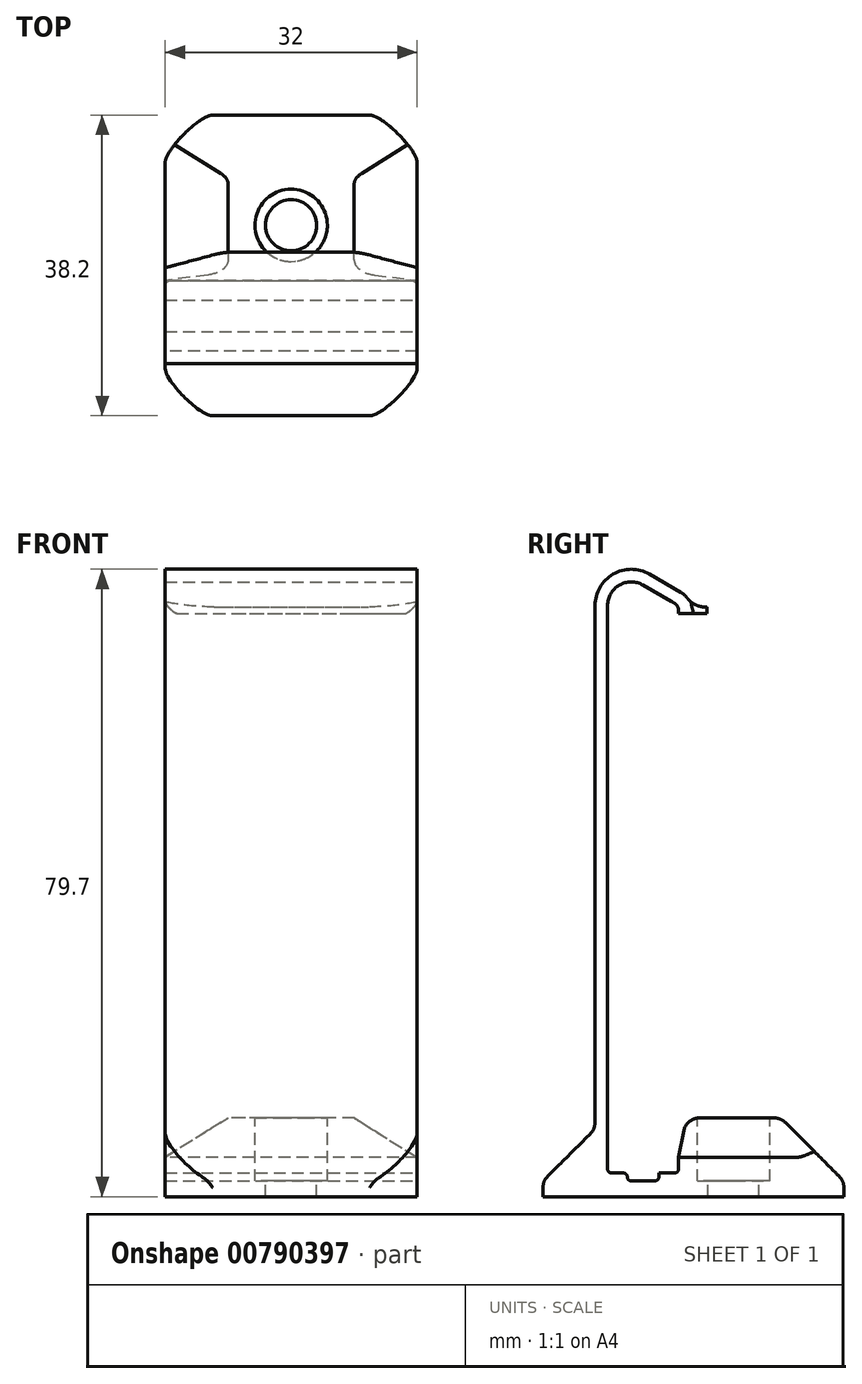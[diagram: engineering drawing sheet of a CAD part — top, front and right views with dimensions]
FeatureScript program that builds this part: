
annotation { "Feature Type Name" : "Feature", "Feature Type Description" : "" }
export const myFeature = defineFeature(function(context is Context, id is Id, definition is map)
    precondition{}
    {
        {
            var Q0;
            Q0=qCreatedBy(makeId("Right.planeOp"),FACE);
            var sketch = newSketch(context, id + "F0", { "sketchPlane" : qUnion([Q0])});
            skLineSegment(sketch, "E0.bottom", {"start": v(-4.5, 0) * mm, "end": v(4.5, 0) * mm});
            skLineSegment(sketch, "E0.top", {"start": v(-4.5, 72.1) * mm, "end": v(4.5, 72.1) * mm});
            skLineSegment(sketch, "E0.left", {"start": v(-4.5, 0) * mm, "end": v(-4.5, 72.1) * mm});
            skLineSegment(sketch, "E0.right", {"start": v(4.5, 0) * mm, "end": v(4.5, 72.1) * mm});
            skSolve(sketch);
        }
        {
            var Q0;
            Q0=qCreatedBy(makeId("Right.planeOp"),FACE);
            var sketch = newSketch(context, id + "F1", { "sketchPlane" : qUnion([Q0])});
            skLineSegment(sketch, "E1", {"start": v(-4.5, 5.6) * mm, "end": v(-6.1, 5.6) * mm});
            skLineSegment(sketch, "E2", {"start": v(-6.1, 5.6) * mm, "end": v(-12.7, -1) * mm});
            skLineSegment(sketch, "E3", {"start": v(-12.7, -1) * mm, "end": v(-12.7, -3) * mm});
            skLineSegment(sketch, "E4", {"start": v(-12.7, -3) * mm, "end": v(25.5, -3) * mm});
            skLineSegment(sketch, "E5", {"start": v(25.5, -3) * mm, "end": v(25.5, -1) * mm});
            skLineSegment(sketch, "E6", {"start": v(25.5, -1) * mm, "end": v(17.5, 7) * mm});
            skLineSegment(sketch, "E7", {"start": v(17.5, 7) * mm, "end": v(4.5, 7) * mm});
            skLineSegment(sketch, "E8", {"start": v(4.5, 7) * mm, "end": v(4.5, 0) * mm});
            skLineSegment(sketch, "E9", {"start": v(4.5, 0) * mm, "end": v(-4.5, 0) * mm});
            skLineSegment(sketch, "E10", {"start": v(-4.5, 0) * mm, "end": v(-4.5, 5.6) * mm});
            skSolve(sketch);
        }
        {
            var Q0;
            Q0=qSketchRegion(id+"F1",true);
            extrude(context, id + "F2", {"entities" : qUnion([Q0]), "endBound" : BoundingType.SYMMETRIC, "depth" : 32 * mm, "offsetDistance" : 25 * mm});
        }
        {
            var Q0;
            Q0=makeQuery(id+"F2.opExtrude","CAP_FACE",FACE,{"disambiguationData":[OSD([sQuery(id+"F1.wireOp",EDGE,"E1"),sQuery(id+"F1.wireOp",EDGE,"E2"),sQuery(id+"F1.wireOp",EDGE,"E3"),sQuery(id+"F1.wireOp",EDGE,"E4"),sQuery(id+"F1.wireOp",EDGE,"E5"),sQuery(id+"F1.wireOp",EDGE,"E6"),sQuery(id+"F1.wireOp",EDGE,"E7"),sQuery(id+"F1.wireOp",EDGE,"E8"),sQuery(id+"F1.wireOp",EDGE,"E9"),sQuery(id+"F1.wireOp",EDGE,"E10")])],"isStart":false});
            var sketch = newSketch(context, id + "F3", { "sketchPlane" : qUnion([Q0])});
            skLineSegment(sketch, "E11", {"start": v(-6.1, 5.6) * mm, "end": v(-4.5, 5.6) * mm});
            skLineSegment(sketch, "E12", {"start": v(-4.5, 5.6) * mm, "end": v(-4.5, 72.1) * mm});
            skLineSegment(sketch, "E13", {"start": v(0, 74.7) * mm, "end": v(4, 72.39) * mm});
            skLineSegment(sketch, "E14", {"start": v(4.5, 71.52) * mm, "end": v(4.5, 71.1) * mm});
            skLineSegment(sketch, "E15", {"start": v(4.5, 71.1) * mm, "end": v(6.1, 71.1) * mm});
            skLineSegment(sketch, "E16", {"start": v(6.1, 71.1) * mm, "end": v(6.1, 71.52) * mm});
            skLineSegment(sketch, "E17", {"start": v(4.8, 73.77) * mm, "end": v(0.8, 76.08) * mm});
            skLineSegment(sketch, "E18", {"start": v(-6.1, 72.1) * mm, "end": v(-6.1, 5.6) * mm});
            skArc(sketch, "E19", {"start": v(0, 74.7) * mm, "mid": v(-3, 74.7) * mm, "end": v(-4.5, 72.1) * mm});
            skArc(sketch, "E20", {"start": v(0.8, 76.08) * mm, "mid": v(-3.8, 76.08) * mm, "end": v(-6.1, 72.1) * mm});
            skArc(sketch, "E21", {"start": v(6.1, 71.52) * mm, "mid": v(5.75, 72.82) * mm, "end": v(4.8, 73.77) * mm});
            skArc(sketch, "E22", {"start": v(4.5, 71.52) * mm, "mid": v(4.37, 72.02) * mm, "end": v(4, 72.39) * mm});
            skLineSegment(sketch, "E23", {"start": v(4, 72.39) * mm, "end": v(4.5, 72.1) * mm, "construction": true});
            skLineSegment(sketch, "E24", {"start": v(4.5, 72.1) * mm, "end": v(4.5, 71.52) * mm, "construction": true});
            skLineSegment(sketch, "E25", {"start": v(4.5, 72.1) * mm, "end": v(-4.5, 72.1) * mm, "construction": true});
            skSolve(sketch);
        }
        {
            var Q0;
            Q0=qSketchRegion(id+"F3",true);
            var Q1;
            Q1=makeQuery(id+"F2.opExtrude","CAP_FACE",FACE,{"disambiguationData":[OSD([sQuery(id+"F1.wireOp",EDGE,"E1"),sQuery(id+"F1.wireOp",EDGE,"E2"),sQuery(id+"F1.wireOp",EDGE,"E3"),sQuery(id+"F1.wireOp",EDGE,"E4"),sQuery(id+"F1.wireOp",EDGE,"E5"),sQuery(id+"F1.wireOp",EDGE,"E6"),sQuery(id+"F1.wireOp",EDGE,"E7"),sQuery(id+"F1.wireOp",EDGE,"E8"),sQuery(id+"F1.wireOp",EDGE,"E9"),sQuery(id+"F1.wireOp",EDGE,"E10")])],"isStart":true});
            extrude(context, id + "F4", {"entities" : qUnion([Q0]), "operationType" : NewBodyOperationType.ADD, "endBound" : BoundingType.UP_TO_SURFACE, "oppositeDirection" : true, "endBoundEntityFace" : qUnion([Q1]), "depth" : 25 * mm});
        }
        {
            var Q0;
            Q0=makeQuery(id+"F4.boolean.opBoolean","MERGE",FACE,{"derivedFrom":[makeQuery(id+"F2.opExtrude","CAP_FACE",FACE,{"disambiguationData":[OSD([sQuery(id+"F1.wireOp",EDGE,"E1"),sQuery(id+"F1.wireOp",EDGE,"E2"),sQuery(id+"F1.wireOp",EDGE,"E3"),sQuery(id+"F1.wireOp",EDGE,"E4"),sQuery(id+"F1.wireOp",EDGE,"E5"),sQuery(id+"F1.wireOp",EDGE,"E6"),sQuery(id+"F1.wireOp",EDGE,"E7"),sQuery(id+"F1.wireOp",EDGE,"E8"),sQuery(id+"F1.wireOp",EDGE,"E9"),sQuery(id+"F1.wireOp",EDGE,"E10")])],"isStart":false}),makeQuery(id+"F4.opExtrude","CAP_FACE",FACE,{"disambiguationData":[OSD([sQuery(id+"F3.wireOp",EDGE,"E11"),sQuery(id+"F3.wireOp",EDGE,"E12"),sQuery(id+"F3.wireOp",EDGE,"E13"),sQuery(id+"F3.wireOp",EDGE,"E14"),sQuery(id+"F3.wireOp",EDGE,"E15"),sQuery(id+"F3.wireOp",EDGE,"E16"),sQuery(id+"F3.wireOp",EDGE,"E17"),sQuery(id+"F3.wireOp",EDGE,"E18"),sQuery(id+"F3.wireOp",EDGE,"E19"),sQuery(id+"F3.wireOp",EDGE,"E20"),sQuery(id+"F3.wireOp",EDGE,"E21"),sQuery(id+"F3.wireOp",EDGE,"E22")])],"isStart":true})]});
            var sketch = newSketch(context, id + "F5", { "sketchPlane" : qUnion([Q0])});
            skLineSegment(sketch, "E26.bottom", {"start": v(-2, 0) * mm, "end": v(2, 0) * mm});
            skLineSegment(sketch, "E26.top", {"start": v(-2, -1) * mm, "end": v(2, -1) * mm});
            skLineSegment(sketch, "E26.left", {"start": v(-2, 0) * mm, "end": v(-2, -1) * mm});
            skLineSegment(sketch, "E26.right", {"start": v(2, 0) * mm, "end": v(2, -1) * mm});
            skLineSegment(sketch, "E27", {"start": v(-4.5, 0) * mm, "end": v(-2, 0) * mm});
            skLineSegment(sketch, "E28", {"start": v(2, 0) * mm, "end": v(4.5, 0) * mm});
            skSolve(sketch);
        }
        {
            var Q0;
            Q0=qSketchRegion(id+"F5",true);
            extrude(context, id + "F6", {"entities" : qUnion([Q0]), "operationType" : NewBodyOperationType.REMOVE, "endBound" : BoundingType.THROUGH_ALL, "oppositeDirection" : true, "depth" : 25 * mm});
        }
        {
            var Q0;
            Q0=makeQuery(id+"F2.opExtrude","SWEPT_EDGE",EDGE,{"disambiguationData":[OSD([sQuery(id+"F1.wireOp",EDGE,"E7"),sQuery(id+"F1.wireOp",EDGE,"E8")])]});
            chamfer(context, id + "F7", {"entities" : qUnion([Q0]), "chamferType" : ChamferType.TWO_OFFSETS, "width1" : 5 * mm, "oppositeDirection" : false, "width2" : 1 * mm, "tangentPropagation" : true});
        }
        {
            var Q0;
            Q0=makeQuery(id+"F2.opExtrude","SWEPT_FACE",FACE,{"disambiguationData":[OSD([sQuery(id+"F1.wireOp",EDGE,"E7")])]});
            var sketch = newSketch(context, id + "F8", { "sketchPlane" : qUnion([Q0])});
            skCircle(sketch, "E29", {"center": v(0, 11.5) * mm, "radius": 4.6 * mm});
            skLineSegment(sketch, "E30", {"start": v(0, 6.9) * mm, "end": v(0, 5.5) * mm, "construction": true});
            skLineSegment(sketch, "E31", {"start": v(0, 16.1) * mm, "end": v(0, 17.5) * mm, "construction": true});
            skSolve(sketch);
        }
        {
            var Q0;
            Q0=qSketchRegion(id+"F8",true);
            extrude(context, id + "F9", {"entities" : qUnion([Q0]), "operationType" : NewBodyOperationType.REMOVE, "oppositeDirection" : true, "depth" : 8 * mm});
        }
        {
            var Q0;
            Q0=makeQuery(id+"F9.boolean.opBoolean","COPY",FACE,{"derivedFrom":makeQuery(id+"F9.opExtrude","CAP_FACE",FACE,{"disambiguationData":[OSD([sQuery(id+"F8.wireOp",EDGE,"E29")])],"isStart":false})});
            var sketch = newSketch(context, id + "F10", { "sketchPlane" : qUnion([Q0])});
            skCircle(sketch, "E32", {"center": v(0, 11.5) * mm, "radius": 3.25 * mm});
            skSolve(sketch);
        }
        {
            var Q0;
            Q0=qSketchRegion(id+"F10",true);
            extrude(context, id + "F11", {"entities" : qUnion([Q0]), "operationType" : NewBodyOperationType.REMOVE, "endBound" : BoundingType.UP_TO_NEXT, "oppositeDirection" : true, "depth" : 25 * mm});
        }
        {
            var Q0;
            Q0=makeQuery(id+"F2.opExtrude","SWEPT_EDGE",EDGE,{"disambiguationData":[OSD([sQuery(id+"F1.wireOp",EDGE,"E9"),sQuery(id+"F1.wireOp",EDGE,"E10")])]});
            var Q1;
            Q1=makeQuery(id+"F2.opExtrude","SWEPT_EDGE",EDGE,{"disambiguationData":[OSD([sQuery(id+"F1.wireOp",EDGE,"E8"),sQuery(id+"F1.wireOp",EDGE,"E9")])]});
            var Q2;
            Q2=makeQuery(id+"F2.opExtrude","SWEPT_EDGE",EDGE,{"disambiguationData":[OSD([sQuery(id+"F1.wireOp",EDGE,"E7"),sQuery(id+"F1.wireOp",EDGE,"E8")])]});
            var Q3;
            Q3=makeQuery(id+"F6.boolean.opBoolean","COPY",EDGE,{"derivedFrom":makeQuery(id+"F6.opExtrude","SWEPT_EDGE",EDGE,{"disambiguationData":[OSD([sQuery(id+"F5.wireOp",EDGE,"E26.top"),sQuery(id+"F5.wireOp",EDGE,"E26.right")])]})});
            var Q4;
            Q4=makeQuery(id+"F6.boolean.opBoolean","COPY",EDGE,{"derivedFrom":makeQuery(id+"F6.opExtrude","SWEPT_EDGE",EDGE,{"disambiguationData":[OSD([sQuery(id+"F5.wireOp",EDGE,"E26.top"),sQuery(id+"F5.wireOp",EDGE,"E26.left")])]})});
            var Q5;
            Q5=makeQuery(id+"F6.boolean.opBoolean","COPY",EDGE,{"derivedFrom":makeQuery(id+"F6.opExtrude","SWEPT_EDGE",EDGE,{"disambiguationData":[OSD([sQuery(id+"F5.wireOp",EDGE,"E26.bottom"),sQuery(id+"F5.wireOp",EDGE,"E26.right"),sQuery(id+"F5.wireOp",EDGE,"E28")])]})});
            var Q6;
            Q6=makeQuery(id+"F6.boolean.opBoolean","COPY",EDGE,{"derivedFrom":makeQuery(id+"F6.opExtrude","SWEPT_EDGE",EDGE,{"disambiguationData":[OSD([sQuery(id+"F5.wireOp",EDGE,"E26.bottom"),sQuery(id+"F5.wireOp",EDGE,"E26.left"),sQuery(id+"F5.wireOp",EDGE,"E27")])]})});
            fillet(context, id + "F12", {"entities" : qUnion([Q0, Q1, Q2, Q3, Q4, Q5, Q6]), "radius" : .5 * mm, "tangentPropagation" : true, "allowEdgeOverflow" : false});
        }
        {
            var Q0;
            Q0=makeQuery(id+"F2.opExtrude","SWEPT_EDGE",EDGE,{"disambiguationData":[OSD([sQuery(id+"F1.wireOp",EDGE,"E5"),sQuery(id+"F1.wireOp",EDGE,"E6")])]});
            var Q1;
            Q1=makeQuery(id+"F2.opExtrude","SWEPT_EDGE",EDGE,{"disambiguationData":[OSD([sQuery(id+"F1.wireOp",EDGE,"E6"),sQuery(id+"F1.wireOp",EDGE,"E7")])]});
            var Q2;
            {var subQ0=sQuery(id+"F1.wireOp",EDGE,"E2");Q2=makeQuery(id+"F4.boolean.opBoolean","MERGE",EDGE,{"derivedFrom":[makeQuery(id+"F2.opExtrude","SWEPT_EDGE",EDGE,{"disambiguationData":[OSD([sQuery(id+"F1.wireOp",EDGE,"E1"),subQ0])]}),makeQuery(id+"F4.opExtrude","SWEPT_EDGE",EDGE,{"disambiguationData":[OSD([subQ0,sQuery(id+"F3.wireOp",EDGE,"E11"),sQuery(id+"F3.wireOp",EDGE,"E18")])]})]});}
            var Q3;
            Q3=makeQuery(id+"F2.opExtrude","SWEPT_EDGE",EDGE,{"disambiguationData":[OSD([sQuery(id+"F1.wireOp",EDGE,"E2"),sQuery(id+"F1.wireOp",EDGE,"E3")])]});
            var Q4;
            {var subQ0=sQuery(id+"F1.wireOp",EDGE,"E7");Q4=makeQuery(id+"F7.opChamfer","BLEND_EDGE",EDGE,{"blendedFrom":[makeQuery(id+"F2.opExtrude","SWEPT_EDGE",EDGE,{"disambiguationData":[OSD([subQ0,sQuery(id+"F1.wireOp",EDGE,"E8")])]}),makeQuery(id+"F2.opExtrude","SWEPT_FACE",FACE,{"disambiguationData":[OSD([subQ0])]})],"blendedInto":[makeQuery(id+"F2.opExtrude","SWEPT_FACE",FACE,{"disambiguationData":[OSD([subQ0])]})]});}
            fillet(context, id + "F13", {"entities" : qUnion([Q0, Q1, Q2, Q3, Q4]), "radius" : 2 * mm, "tangentPropagation" : true, "allowEdgeOverflow" : false});
        }
        {
            var Q0;
            Q0=makeQuery(id+"F2.opExtrude","CAP_EDGE",EDGE,{"disambiguationData":[OSD([sQuery(id+"F1.wireOp",EDGE,"E3")])],"isStart":false});
            var Q1;
            Q1=makeQuery(id+"F2.opExtrude","CAP_EDGE",EDGE,{"disambiguationData":[OSD([sQuery(id+"F1.wireOp",EDGE,"E5")])],"isStart":false});
            var Q2;
            Q2=makeQuery(id+"F2.opExtrude","CAP_EDGE",EDGE,{"disambiguationData":[OSD([sQuery(id+"F1.wireOp",EDGE,"E5")])],"isStart":true});
            var Q3;
            Q3=makeQuery(id+"F2.opExtrude","CAP_EDGE",EDGE,{"disambiguationData":[OSD([sQuery(id+"F1.wireOp",EDGE,"E3")])],"isStart":true});
            fillet(context, id + "F14", {"entities" : qUnion([Q0, Q1, Q2, Q3]), "radius" : 6 * mm, "rho" : .2, "crossSection" : FilletCrossSection.CONIC, "allowEdgeOverflow" : false});
        }
        {
            var Q0;
            Q0=makeQuery(id+"F2.opExtrude","CAP_EDGE",EDGE,{"disambiguationData":[OSD([sQuery(id+"F1.wireOp",EDGE,"E7")])],"isStart":true});
            var Q1;
            Q1=makeQuery(id+"F2.opExtrude","CAP_EDGE",EDGE,{"disambiguationData":[OSD([sQuery(id+"F1.wireOp",EDGE,"E7")])],"isStart":false});
            chamfer(context, id + "F15", {"entities" : qUnion([Q0, Q1]), "chamferType" : ChamferType.TWO_OFFSETS, "width1" : 8 * mm, "oppositeDirection" : false, "width2" : 5 * mm});
        }
        {
            var Q0;
            Q0=makeQuery(id+"F4.opExtrude","SWEPT_FACE",FACE,{"disambiguationData":[OSD([sQuery(id+"F3.wireOp",EDGE,"E15")])]});
            var sketch = newSketch(context, id + "F16", { "sketchPlane" : qUnion([Q0])});
            skLineSegment(sketch, "E33", {"start": v(-16, -6.1) * mm, "end": v(-9.8, -7.76) * mm});
            skLineSegment(sketch, "E34", {"start": v(-7.22, -8.1) * mm, "end": v(7.22, -8.1) * mm});
            skLineSegment(sketch, "E35", {"start": v(9.8, -7.76) * mm, "end": v(16, -6.1) * mm});
            skPoint(sketch, "E36.visualSharp", {"position": v(8.54, -8.1) * mm});
            skArc(sketch, "E36.filletArc", {"start": v(7.22, -8.1) * mm, "mid": v(8.52, -8.01) * mm, "end": v(9.8, -7.76) * mm});
            skPoint(sketch, "E37.visualSharp", {"position": v(-8.54, -8.1) * mm});
            skArc(sketch, "E37.filletArc", {"start": v(-9.8, -7.76) * mm, "mid": v(-8.52, -8.01) * mm, "end": v(-7.22, -8.1) * mm});
            skLineSegment(sketch, "E38", {"start": v(16, -6.1) * mm, "end": v(16, -4.5) * mm});
            skLineSegment(sketch, "E39", {"start": v(16, -4.5) * mm, "end": v(-16, -4.5) * mm});
            skLineSegment(sketch, "E40", {"start": v(-16, -4.5) * mm, "end": v(-16, -6.1) * mm});
            skSolve(sketch);
        }
        {
            var Q0;
            Q0=qSketchRegion(id+"F16",true);
            extrude(context, id + "F17", {"entities" : qUnion([Q0]), "operationType" : NewBodyOperationType.ADD, "oppositeDirection" : true, "depth" : .8 * mm});
        }
        {
            var Q0;
            Q0=makeQuery(id+"F17.boolean.opBoolean","INTERSECT",EDGE,{"derivedFrom":[makeQuery(id+"F4.opExtrude","SWEPT_FACE",FACE,{"disambiguationData":[OSD([sQuery(id+"F3.wireOp",EDGE,"E21")])]}),makeQuery(id+"F17.opExtrude","CAP_FACE",FACE,{"disambiguationData":[OSD([sQuery(id+"F16.wireOp",EDGE,"E33"),sQuery(id+"F16.wireOp",EDGE,"E34"),sQuery(id+"F16.wireOp",EDGE,"E35"),sQuery(id+"F16.wireOp",EDGE,"E36.filletArc"),sQuery(id+"F16.wireOp",EDGE,"E37.filletArc"),sQuery(id+"F16.wireOp",EDGE,"E38"),sQuery(id+"F16.wireOp",EDGE,"E39"),sQuery(id+"F16.wireOp",EDGE,"E40")])],"isStart":false})]});
            fillet(context, id + "F18", {"entities" : qUnion([Q0]), "radius" : 3 * mm, "tangentPropagation" : true, "allowEdgeOverflow" : false});
        }
        {
            var Q0;
            Q0=makeQuery(id+"F4.opExtrude","CAP_EDGE",EDGE,{"disambiguationData":[OSD([sQuery(id+"F3.wireOp",EDGE,"E15")])],"isStart":true});
            var Q1;
            Q1=makeQuery(id+"F4.opExtrude","CAP_EDGE",EDGE,{"disambiguationData":[OSD([sQuery(id+"F3.wireOp",EDGE,"E15")])],"isStart":false});
            fillet(context, id + "F19", {"entities" : qUnion([Q0, Q1]), "radius" : 1.5 * mm, "tangentPropagation" : true, "rho" : .2, "crossSection" : FilletCrossSection.CONIC, "allowEdgeOverflow" : false});
        }
    });
